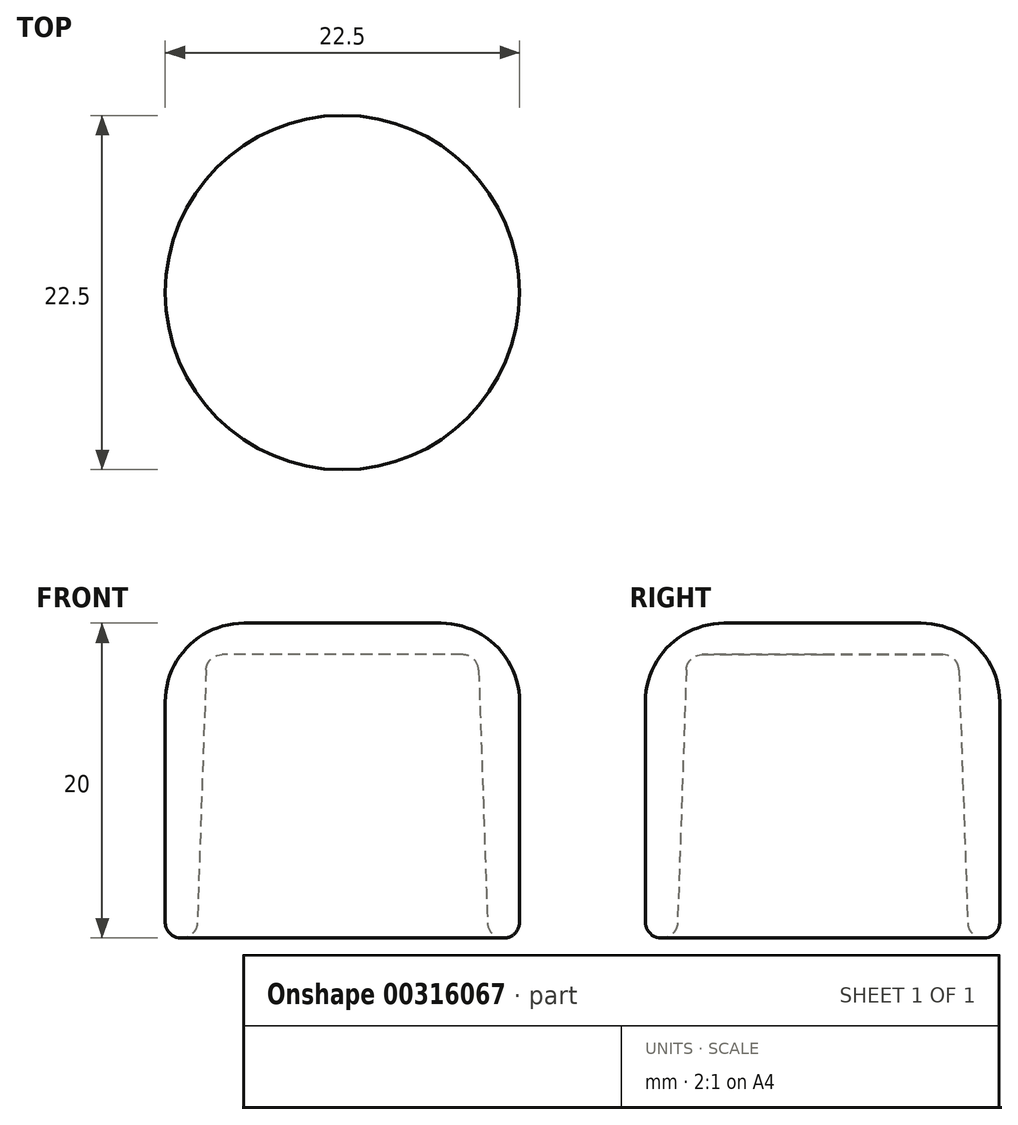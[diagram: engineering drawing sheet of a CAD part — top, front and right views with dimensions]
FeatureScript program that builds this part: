
annotation { "Feature Type Name" : "Feature", "Feature Type Description" : "" }
export const myFeature = defineFeature(function(context is Context, id is Id, definition is map)
    precondition{}
    {
        {
            var Q0;
            Q0=qCreatedBy(makeId("Top.planeOp"),FACE);
            var sketch = newSketch(context, id + "F0", { "sketchPlane" : qUnion([Q0])});
            skCircle(sketch, "E0", {"center": v(0, 0) * mm, "radius": 9.25 * mm});
            skCircle(sketch, "E1.0", {"center": v(0, 0) * mm, "radius": 11.25 * mm});
            skSolve(sketch);
        }
        {
            var Q0;
            Q0=makeQuery(id+"F0.imprint","IMPRINT",FACE,{"disambiguationData":[TD([[makeQuery(id+"F0.imprint","IMPRINT",EDGE,{"derivedFrom":sQuery(id+"F0.wireOp",EDGE,"E0")}),-1.0]])]});
            var Q1;
            Q1=makeQuery(id+"F0.imprint","IMPRINT",FACE,{"disambiguationData":[TD([[makeQuery(id+"F0.imprint","IMPRINT",EDGE,{"derivedFrom":sQuery(id+"F0.wireOp",EDGE,"E0")}),1.0]])]});
            extrude(context, id + "F1", {"entities" : qUnion([Q0, Q1]), "depth" : 20 * mm});
        }
        {
            var Q0;
            Q0=makeQuery(id+"F0.imprint","IMPRINT",FACE,{"disambiguationData":[TD([[makeQuery(id+"F0.imprint","IMPRINT",EDGE,{"derivedFrom":sQuery(id+"F0.wireOp",EDGE,"E0")}),1.0]])]});
            extrude(context, id + "F2", {"entities" : qUnion([Q0]), "operationType" : NewBodyOperationType.REMOVE, "depth" : 18 * mm, "hasDraft" : true, "draftAngle" : 2 * degree, "draftPullDirection" : true});
        }
        {
            var Q0;
            Q0=makeQuery(id+"F1.opExtrude","CAP_EDGE",EDGE,{"disambiguationData":[OSD([sQuery(id+"F0.wireOp",EDGE,"E1.0")])],"isStart":false});
            fillet(context, id + "F3", {"entities" : qUnion([Q0]), "radius" : 5 * mm, "tangentPropagation" : true, "allowEdgeOverflow" : false});
        }
        {
            var Q0;
            Q0=makeQuery(id+"F1.opExtrude","SWEPT_FACE",FACE,{"disambiguationData":[OSD([sQuery(id+"F0.wireOp",EDGE,"E1.0")])]});
            var Q1;
            Q1=makeQuery(id+"F2.boolean.opBoolean","COPY",FACE,{"derivedFrom":makeQuery(id+"F2.opExtrude","SWEPT_FACE",FACE,{"disambiguationData":[OSD([sQuery(id+"F0.wireOp",EDGE,"E0")])]})});
            var Q2;
            Q2=makeQuery(id+"F1.opExtrude","CAP_EDGE",EDGE,{"disambiguationData":[OSD([sQuery(id+"F0.wireOp",EDGE,"E1.0")])],"isStart":true});
            fillet(context, id + "F4", {"entities" : qUnion([Q0, Q1, Q2]), "radius" : 1 * mm, "tangentPropagation" : true, "allowEdgeOverflow" : false});
        }
    });
